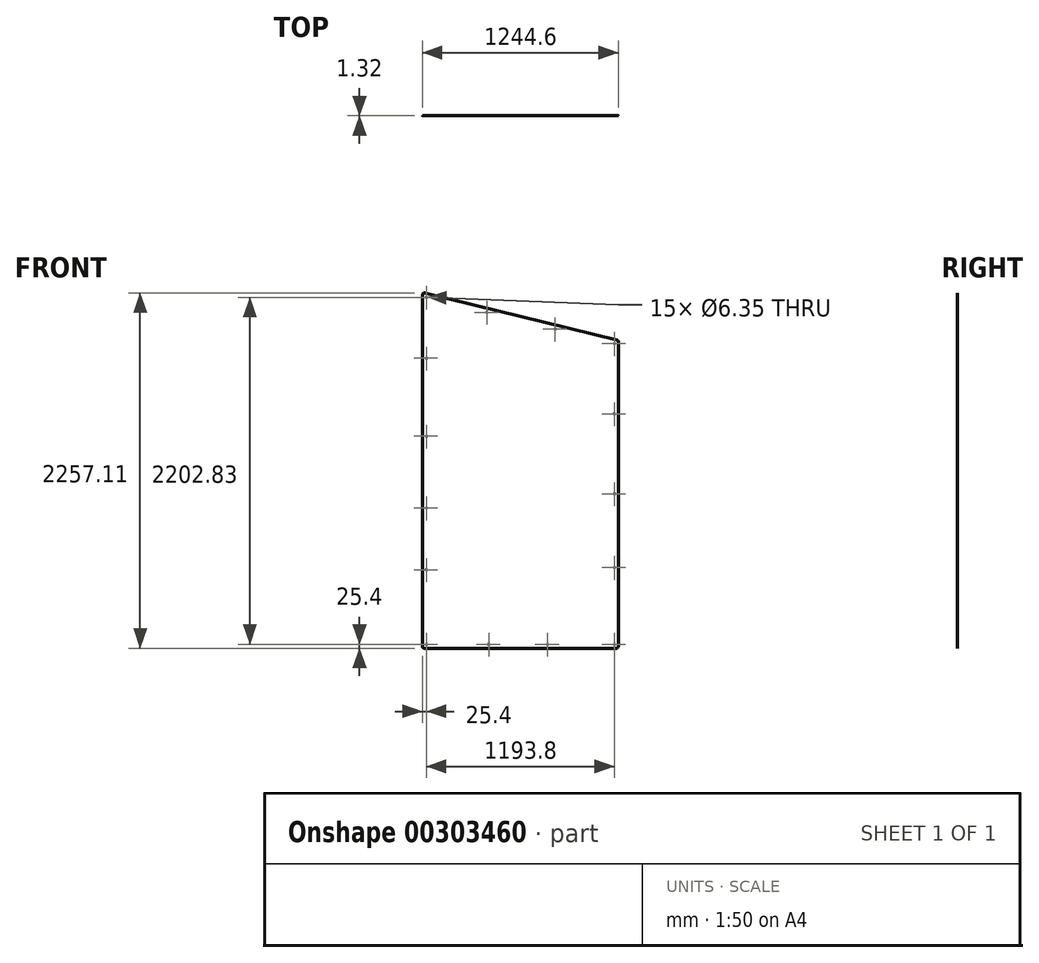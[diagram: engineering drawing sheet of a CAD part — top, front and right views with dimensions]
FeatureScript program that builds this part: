
annotation { "Feature Type Name" : "Feature", "Feature Type Description" : "" }
export const myFeature = defineFeature(function(context is Context, id is Id, definition is map)
    precondition{}
    {
        {
            var Q0;
            Q0=qCreatedBy(makeId("Front.planeOp"),FACE);
            var sketch = newSketch(context, id + "F0", { "sketchPlane" : qUnion([Q0])});
            skLineSegment(sketch, "E0", {"start": v(0, 0) * mm, "end": v(1244.6, 0) * mm});
            skLineSegment(sketch, "E1", {"start": v(1244.6, 0) * mm, "end": v(1244.6, 1955.8) * mm});
            skLineSegment(sketch, "E2", {"start": v(1244.6, 1955.8) * mm, "end": v(0, 2260.6) * mm});
            skLineSegment(sketch, "E3", {"start": v(0, 2260.6) * mm, "end": v(0, 0) * mm});
            skSolve(sketch);
        }
        {
            var Q0;
            Q0=qSketchRegion(id+"F0",true);
            extrude(context, id + "F1", {"entities" : qUnion([Q0]), "depth" : 1.32 * mm});
        }
        {
            var Q0;
            Q0=makeQuery(id+"F1.opExtrude","CAP_FACE",FACE,{"disambiguationData":[OSD([sQuery(id+"F0.wireOp",EDGE,"E0"),sQuery(id+"F0.wireOp",EDGE,"E1"),sQuery(id+"F0.wireOp",EDGE,"E2"),sQuery(id+"F0.wireOp",EDGE,"E3")])],"isStart":false});
            var sketch = newSketch(context, id + "F2", { "sketchPlane" : qUnion([Q0])});
            skLineSegment(sketch, "E4.0", {"start": v(1219.2, 1935.87) * mm, "end": v(25.4, 2228.23) * mm, "construction": true});
            skLineSegment(sketch, "E4.1", {"start": v(1219.2, 25.4) * mm, "end": v(1219.2, 1935.87) * mm, "construction": true});
            skLineSegment(sketch, "E4.2", {"start": v(25.4, 25.4) * mm, "end": v(1219.2, 25.4) * mm, "construction": true});
            skLineSegment(sketch, "E4.3", {"start": v(25.4, 2228.23) * mm, "end": v(25.4, 25.4) * mm, "construction": true});
            skCircle(sketch, "E5", {"center": v(25.4, 2228.23) * mm, "radius": 3.18 * mm});
            skCircle(sketch, "E6", {"center": v(1219.2, 1935.87) * mm, "radius": 3.18 * mm});
            skCircle(sketch, "E7", {"center": v(410.44, 2133.93) * mm, "radius": 3.18 * mm});
            skCircle(sketch, "E8", {"center": v(843.36, 2027.91) * mm, "radius": 3.18 * mm});
            skCircle(sketch, "E9", {"center": v(1219.2, 25.4) * mm, "radius": 3.18 * mm});
            skCircle(sketch, "E10", {"center": v(25.4, 25.4) * mm, "radius": 3.18 * mm});
            skCircle(sketch, "E11", {"center": v(421.26, 25.4) * mm, "radius": 3.18 * mm});
            skCircle(sketch, "E12", {"center": v(794.35, 25.4) * mm, "radius": 3.18 * mm});
            skCircle(sketch, "E13", {"center": v(1219.2, 980.63) * mm, "radius": 3.18 * mm});
            skCircle(sketch, "E14", {"center": v(1219.2, 1489.18) * mm, "radius": 3.18 * mm});
            skCircle(sketch, "E15", {"center": v(1219.2, 513.28) * mm, "radius": 3.18 * mm});
            skCircle(sketch, "E16", {"center": v(25.4, 1346.96) * mm, "radius": 3.18 * mm});
            skCircle(sketch, "E17", {"center": v(25.4, 890.89) * mm, "radius": 3.18 * mm});
            skCircle(sketch, "E18", {"center": v(25.4, 498.57) * mm, "radius": 3.18 * mm});
            skCircle(sketch, "E19", {"center": v(25.4, 1842.27) * mm, "radius": 3.18 * mm});
            skLineSegment(sketch, "E20", {"start": v(25.4, 1842.27) * mm, "end": v(-402.1, 1842.27) * mm, "construction": true});
            skLineSegment(sketch, "E21", {"start": v(25.4, 1346.96) * mm, "end": v(-407, 1346.96) * mm, "construction": true});
            skLineSegment(sketch, "E22", {"start": v(25.4, 890.89) * mm, "end": v(-392.28, 890.89) * mm, "construction": true});
            skLineSegment(sketch, "E23", {"start": v(-397.19, 498.57) * mm, "end": v(25.4, 498.57) * mm, "construction": true});
            skLineSegment(sketch, "E24", {"start": v(410.44, 2133.93) * mm, "end": v(485.54, 2440.56) * mm, "construction": true});
            skLineSegment(sketch, "E25", {"start": v(902.38, 2268.92) * mm, "end": v(843.36, 2027.91) * mm, "construction": true});
            skLineSegment(sketch, "E26", {"start": v(1219.2, 1489.18) * mm, "end": v(1510.47, 1489.18) * mm, "construction": true});
            skLineSegment(sketch, "E27", {"start": v(1554.6, 513.28) * mm, "end": v(1219.2, 513.28) * mm, "construction": true});
            skLineSegment(sketch, "E28", {"start": v(794.35, 25.4) * mm, "end": v(794.35, -298.08) * mm, "construction": true});
            skLineSegment(sketch, "E29", {"start": v(421.26, -325.82) * mm, "end": v(421.26, 25.4) * mm, "construction": true});
            skSolve(sketch);
        }
        {
            var Q0;
            Q0=qSketchRegion(id+"F2",true);
            extrude(context, id + "F3", {"entities" : qUnion([Q0]), "operationType" : NewBodyOperationType.REMOVE, "oppositeDirection" : true, "depth" : 25.4 * mm});
        }
        {
            var Q0;
            Q0=makeQuery(id+"F1.opExtrude","SWEPT_EDGE",EDGE,{"disambiguationData":[OSD([sQuery(id+"F0.wireOp",EDGE,"E1"),sQuery(id+"F0.wireOp",EDGE,"E2")])]});
            var Q1;
            Q1=makeQuery(id+"F1.opExtrude","SWEPT_EDGE",EDGE,{"disambiguationData":[OSD([sQuery(id+"F0.wireOp",EDGE,"E2"),sQuery(id+"F0.wireOp",EDGE,"E3")])]});
            var Q2;
            Q2=makeQuery(id+"F1.opExtrude","SWEPT_EDGE",EDGE,{"disambiguationData":[OSD([sQuery(id+"F0.wireOp",EDGE,"E0"),sQuery(id+"F0.wireOp",EDGE,"E1")])]});
            var Q3;
            Q3=makeQuery(id+"F1.opExtrude","SWEPT_EDGE",EDGE,{"disambiguationData":[OSD([sQuery(id+"F0.wireOp",EDGE,"E0"),sQuery(id+"F0.wireOp",EDGE,"E3")])]});
            fillet(context, id + "F4", {"entities" : qUnion([Q0, Q1, Q2, Q3]), "radius" : 12.7 * mm, "tangentPropagation" : true, "allowEdgeOverflow" : false});
        }
    });
